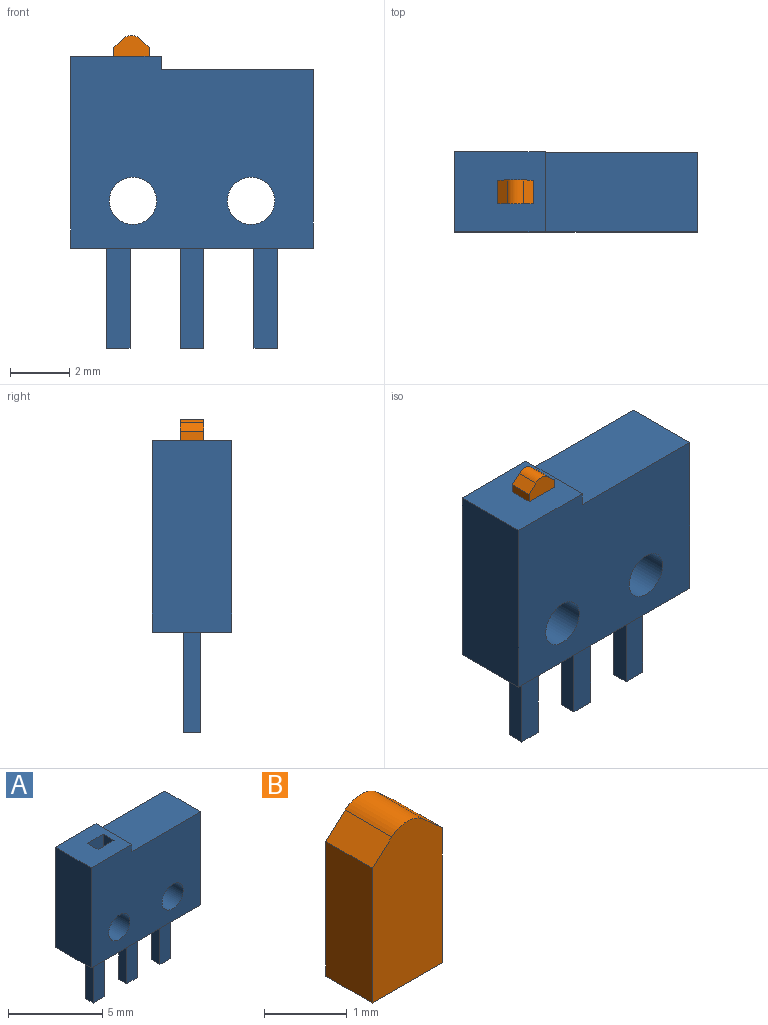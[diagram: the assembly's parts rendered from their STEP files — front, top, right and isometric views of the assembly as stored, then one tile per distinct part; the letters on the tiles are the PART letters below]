
ASSEMBLY  parts=2 mates=1
PART A: 30 faces, bbox 8.2x2.7x9.9 mm
  f0: plane 2.7x0.45mm, normal (1,0,0), area 1.2mm2, adj f1,f2,f3,f4
  f1: plane 8.2x6.5mm, normal (0,-1,0), area 47mm2, adj f0,f3,f4,f5,f6,f7,f8,f9
  f2: plane 8.2x6.5mm, normal (0,1,0), area 47mm2, adj f0,f3,f4,f5,f6,f7,f8,f9
  f3: plane 5.15x2.7mm, normal (0,0,1), area 13.9mm2, adj f0,f1,f2,f9
  f4: plane 3.05x2.7mm, normal (0,0,1), area 7.3mm2, adj f0,f1,f2,f7,f10,f11,f12,f13
  f5: cylinder r=0.8mm len=2.7mm, axis (0,-1,0), area 13.6mm2, adj f1,f2
  f6: plane 8.2x2.7mm, normal (0,0,-1), area 20.7mm2, adj f1,f2,f7,f9,f14,f15,f16,f17
  f7: plane 6.5x2.7mm, normal (-1,0,0), area 17.6mm2, adj f1,f2,f4,f6
  f8: cylinder r=0.8mm len=2.7mm, axis (0,-1,0), area 13.6mm2, adj f1,f2
  f9: plane 6.05x2.7mm, normal (1,0,0), area 16.3mm2, adj f1,f2,f3,f6
  f10: plane 1.6x1.2mm, normal (0,-1,0), area 1.9mm2, adj f4,f11,f12,f26
  f11: plane 1.6x0.8mm, normal (1,0,0), area 1.3mm2, adj f4,f10,f13,f26
  f12: plane 1.6x0.8mm, normal (-1,0,0), area 1.3mm2, adj f4,f10,f13,f26
  f13: plane 1.6x1.2mm, normal (0,1,0), area 1.9mm2, adj f4,f11,f12,f26
  f14: plane 3.4x0.6mm, normal (-1,0,0), area 2mm2, adj f6,f20,f25,f27
  f15: plane 3.4x0.6mm, normal (-1,0,0), area 2mm2, adj f6,f22,f24,f28
  f16: plane 3.4x0.6mm, normal (-1,0,0), area 2mm2, adj f6,f17,f19,f29
  f17: plane 3.4x0.8mm, normal (0,1,0), area 2.7mm2, adj f6,f16,f18,f29
  f18: plane 3.4x0.6mm, normal (1,0,0), area 2mm2, adj f6,f17,f19,f29
  f19: plane 3.4x0.8mm, normal (0,-1,0), area 2.7mm2, adj f6,f16,f18,f29
  f20: plane 3.4x0.8mm, normal (0,-1,0), area 2.7mm2, adj f6,f14,f23,f27
  f21: plane 3.4x0.6mm, normal (1,0,0), area 2mm2, adj f6,f22,f24,f28
  f22: plane 3.4x0.8mm, normal (0,-1,0), area 2.7mm2, adj f6,f15,f21,f28
  f23: plane 3.4x0.6mm, normal (1,0,0), area 2mm2, adj f6,f20,f25,f27
  f24: plane 3.4x0.8mm, normal (0,1,0), area 2.7mm2, adj f6,f15,f21,f28
  f25: plane 3.4x0.8mm, normal (0,1,0), area 2.7mm2, adj f6,f14,f23,f27
  f26: plane 1.2x0.8mm, normal (0,0,1), area 1mm2, adj f10,f11,f12,f13
  f27: plane 0.8x0.6mm, normal (0,0,-1), area 0.5mm2, adj f14,f20,f23,f25
  f28: plane 0.8x0.6mm, normal (0,0,-1), area 0.5mm2, adj f15,f21,f22,f24
  f29: plane 0.8x0.6mm, normal (0,0,-1), area 0.5mm2, adj f16,f17,f18,f19
PART B: 8 faces, bbox 1.2x0.8x2.4 mm
  f0: plane 1.2x0.8mm, normal (0,0,-1), area 1mm2, adj f1,f2,f3,f4
  f1: plane 2.4x1.2mm, normal (0,-1,0), area 2.7mm2, adj f0,f2,f4,f5,f6,f7
  f2: plane 2x0.8mm, normal (1,0,0), area 1.6mm2, adj f0,f1,f3,f5
  f3: plane 2.4x1.2mm, normal (0,1,0), area 2.7mm2, adj f0,f2,f4,f5,f6,f7
  f4: plane 2x0.8mm, normal (-1,0,0), area 1.6mm2, adj f0,f1,f3,f7
  f5: plane 0.8x0.33mm, normal (0.67,0,0.75), area 0.4mm2, adj f1,f2,f3,f6
  f6: cylinder r=0.4mm len=0.8mm, axis (0,1,0), area 0.5mm2, adj f1,f3,f5,f7
  f7: plane 0.8x0.33mm, normal (-0.67,0,0.75), area 0.4mm2, adj f1,f3,f4,f6
PLACE A t=(0,0,-0.74)mm
PLACE B t=(-4.05,0,4.86)mm
MATE slider A.f26 <-> B.f0  axis (0,0,1) through (-3.45,-0.4,2.56)mm
